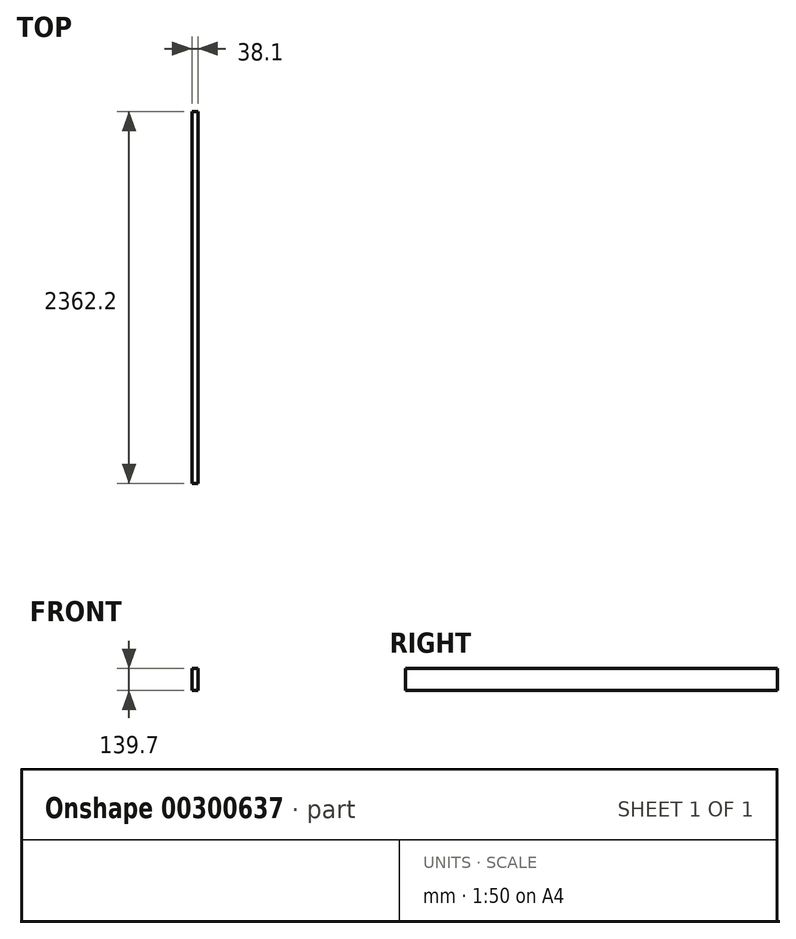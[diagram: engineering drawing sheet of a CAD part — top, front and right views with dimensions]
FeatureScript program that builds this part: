
annotation { "Feature Type Name" : "Feature", "Feature Type Description" : "" }
export const myFeature = defineFeature(function(context is Context, id is Id, definition is map)
    precondition{}
    {
        {
            var Q0;
            Q0=qCreatedBy(makeId("Front.planeOp"),FACE);
            var sketch = newSketch(context, id + "F0", { "sketchPlane" : qUnion([Q0])});
            skLineSegment(sketch, "E0.bottom", {"start": v(19.05, 69.85) * mm, "end": v(-19.05, 69.85) * mm});
            skLineSegment(sketch, "E0.top", {"start": v(19.05, -69.85) * mm, "end": v(-19.05, -69.85) * mm});
            skLineSegment(sketch, "E0.left", {"start": v(19.05, 69.85) * mm, "end": v(19.05, -69.85) * mm});
            skLineSegment(sketch, "E0.right", {"start": v(-19.05, 69.85) * mm, "end": v(-19.05, -69.85) * mm});
            skPoint(sketch, "E0.middle", {"position": v(0, 0) * mm});
            skSolve(sketch);
        }
        {
            var Q0;
            Q0 = qSketchRegion(id + "F0", true);
            extrude(context, id + "F1", {"entities" : qUnion([Q0]), "oppositeDirection" : true, "depth" : 2362.2 * mm});
        }
    });
